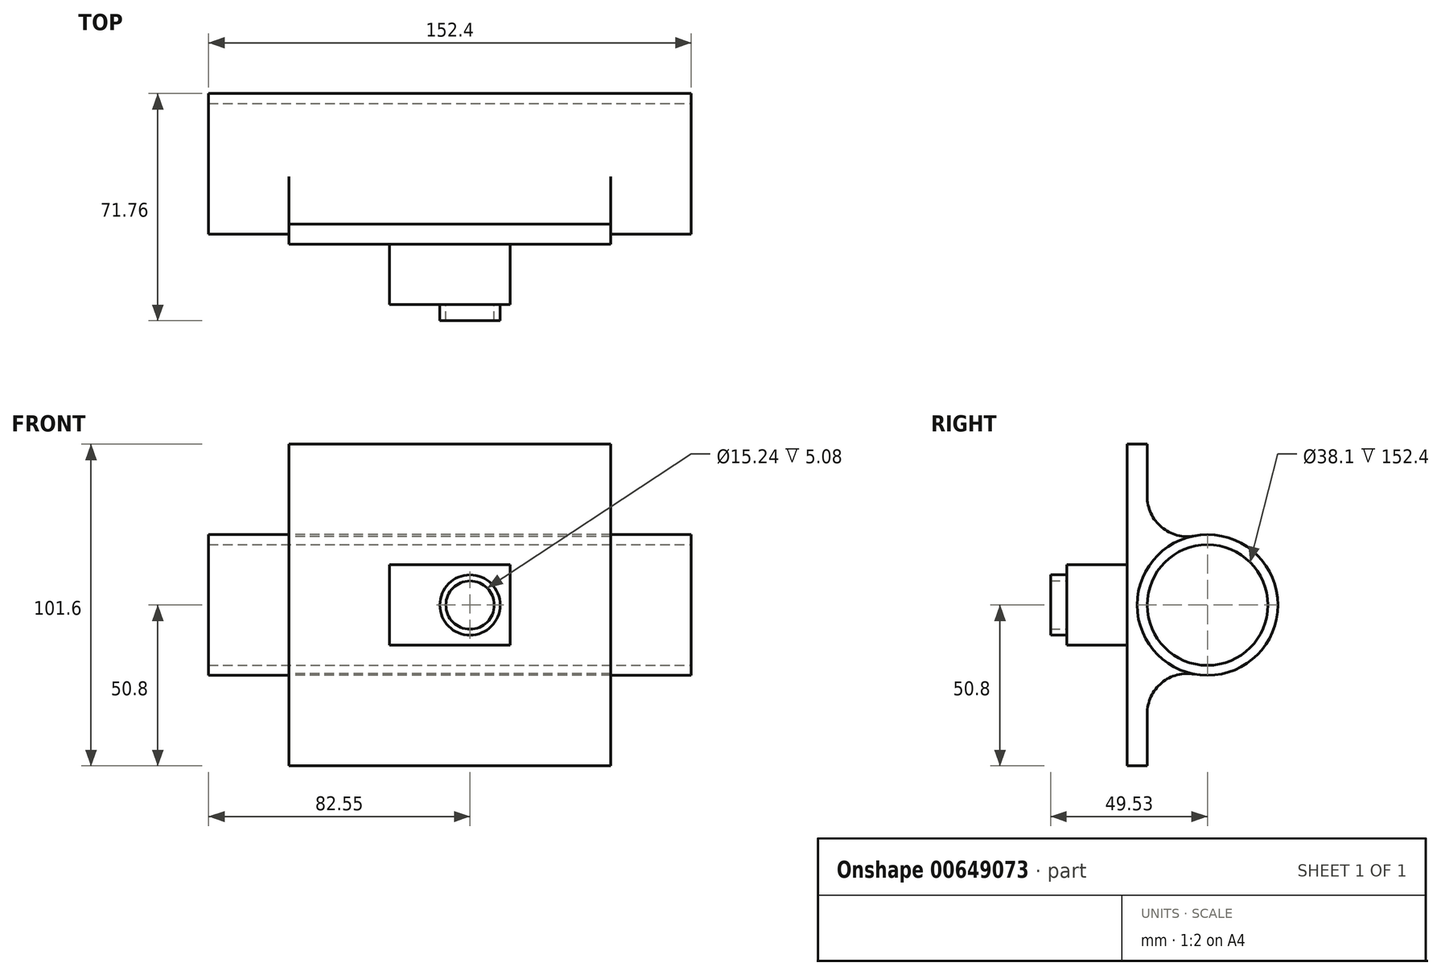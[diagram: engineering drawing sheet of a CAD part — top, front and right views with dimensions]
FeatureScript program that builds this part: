
annotation { "Feature Type Name" : "Feature", "Feature Type Description" : "" }
export const myFeature = defineFeature(function(context is Context, id is Id, definition is map)
    precondition{}
    {
        {
            var Q0;
            Q0=qCreatedBy(makeId("Right.planeOp"),FACE);
            var sketch = newSketch(context, id + "F0", { "sketchPlane" : qUnion([Q0])});
            skCircle(sketch, "E0", {"center": v(0, 0) * mm, "radius": 22.23 * mm});
            skSolve(sketch);
        }
        {
            var Q0;
            Q0 = qSketchRegion(id + "F0", true);
            extrude(context, id + "F1", {"entities" : qUnion([Q0]), "depth" : 76.2 * mm, "offsetDistance" : 25.4 * mm, "hasSecondDirection" : true, "secondDirectionOppositeDirection" : true, "secondDirectionDepth" : 76.2 * mm});
        }
        {
            var Q0;
            Q0=qCreatedBy(makeId("Front.planeOp"),FACE);
            var sketch = newSketch(context, id + "F2", { "sketchPlane" : qUnion([Q0])});
            skLineSegment(sketch, "E1.bottom", {"start": v(-50.8, -50.8) * mm, "end": v(50.8, -50.8) * mm});
            skLineSegment(sketch, "E1.top", {"start": v(-50.8, 50.8) * mm, "end": v(50.8, 50.8) * mm});
            skLineSegment(sketch, "E1.left", {"start": v(-50.8, -50.8) * mm, "end": v(-50.8, 50.8) * mm});
            skLineSegment(sketch, "E1.right", {"start": v(50.8, -50.8) * mm, "end": v(50.8, 50.8) * mm});
            skSolve(sketch);
        }
        {
            var Q0;
            Q0 = qSketchRegion(id + "F2", true);
            extrude(context, id + "F3", {"entities" : qUnion([Q0]), "operationType" : NewBodyOperationType.ADD, "depth" : 25.4 * mm, "offsetDistance" : 25.4 * mm, "hasSecondDirection" : true, "secondDirectionOppositeDirection" : false, "secondDirectionDepth" : 19.05 * mm});
        }
        {
            var Q0;
            Q0=makeQuery(id+"F3.boolean.opBoolean","INTERSECT",EDGE,{"disambiguationData":[OD(1.0)],"derivedFrom":[makeQuery(id+"F1.opExtrude","SWEPT_FACE",FACE,{"disambiguationData":[OSD([sQuery(id+"F0.wireOp",EDGE,"E0")])]}),makeQuery(id+"F3.opExtrude","CAP_FACE",FACE,{"disambiguationData":[OSD([sQuery(id+"F2.wireOp",EDGE,"E1.bottom"),sQuery(id+"F2.wireOp",EDGE,"E1.top"),sQuery(id+"F2.wireOp",EDGE,"E1.left"),sQuery(id+"F2.wireOp",EDGE,"E1.right")])],"isStart":true})]});
            var Q1;
            Q1=makeQuery(id+"F3.boolean.opBoolean","INTERSECT",EDGE,{"disambiguationData":[OD(0.0)],"derivedFrom":[makeQuery(id+"F1.opExtrude","SWEPT_FACE",FACE,{"disambiguationData":[OSD([sQuery(id+"F0.wireOp",EDGE,"E0")])]}),makeQuery(id+"F3.opExtrude","CAP_FACE",FACE,{"disambiguationData":[OSD([sQuery(id+"F2.wireOp",EDGE,"E1.bottom"),sQuery(id+"F2.wireOp",EDGE,"E1.top"),sQuery(id+"F2.wireOp",EDGE,"E1.left"),sQuery(id+"F2.wireOp",EDGE,"E1.right")])],"isStart":true})]});
            fillet(context, id + "F4", {"entities" : qUnion([Q0, Q1]), "radius" : 12.7 * mm, "tangentPropagation" : true, "allowEdgeOverflow" : false});
        }
        {
            var Q0;
            Q0=makeQuery(id+"F3.opExtrude","CAP_FACE",FACE,{"disambiguationData":[OSD([sQuery(id+"F2.wireOp",EDGE,"E1.bottom"),sQuery(id+"F2.wireOp",EDGE,"E1.top"),sQuery(id+"F2.wireOp",EDGE,"E1.left"),sQuery(id+"F2.wireOp",EDGE,"E1.right")])],"isStart":false});
            var sketch = newSketch(context, id + "F5", { "sketchPlane" : qUnion([Q0])});
            skLineSegment(sketch, "E2.bottom", {"start": v(-19.05, -12.7) * mm, "end": v(19.05, -12.7) * mm});
            skLineSegment(sketch, "E2.top", {"start": v(-19.05, 12.7) * mm, "end": v(19.05, 12.7) * mm});
            skLineSegment(sketch, "E2.left", {"start": v(-19.05, -12.7) * mm, "end": v(-19.05, 12.7) * mm});
            skLineSegment(sketch, "E2.right", {"start": v(19.05, -12.7) * mm, "end": v(19.05, 12.7) * mm});
            skSolve(sketch);
        }
        {
            var Q0;
            Q0 = qSketchRegion(id + "F5", true);
            extrude(context, id + "F6", {"entities" : qUnion([Q0]), "operationType" : NewBodyOperationType.ADD, "depth" : 19.05 * mm, "offsetDistance" : 25.4 * mm});
        }
        {
            var Q0;
            Q0=makeQuery(id+"F6.opExtrude","CAP_FACE",FACE,{"disambiguationData":[OSD([sQuery(id+"F5.wireOp",EDGE,"E2.bottom"),sQuery(id+"F5.wireOp",EDGE,"E2.top"),sQuery(id+"F5.wireOp",EDGE,"E2.left"),sQuery(id+"F5.wireOp",EDGE,"E2.right")])],"isStart":false});
            var sketch = newSketch(context, id + "F7", { "sketchPlane" : qUnion([Q0])});
            skCircle(sketch, "E3", {"center": v(6.35, 0) * mm, "radius": 9.53 * mm});
            skCircle(sketch, "E4", {"center": v(6.35, 0) * mm, "radius": 7.62 * mm});
            skSolve(sketch);
        }
        {
            var Q0;
            Q0 = qSketchRegion(id + "F7", true);
            extrude(context, id + "F8", {"entities" : qUnion([Q0]), "operationType" : NewBodyOperationType.ADD, "depth" : 5.08 * mm, "offsetDistance" : 25.4 * mm});
        }
        {
            var Q0;
            Q0=makeQuery(id+"F1.opExtrude","CAP_FACE",FACE,{"disambiguationData":[OSD([sQuery(id+"F0.wireOp",EDGE,"E0")])],"isStart":false});
            var sketch = newSketch(context, id + "F9", { "sketchPlane" : qUnion([Q0])});
            skCircle(sketch, "E5", {"center": v(0, 0) * mm, "radius": 19.05 * mm});
            skSolve(sketch);
        }
        {
            var Q0;
            Q0 = qSketchRegion(id + "F9", true);
            extrude(context, id + "F10", {"entities" : qUnion([Q0]), "operationType" : NewBodyOperationType.REMOVE, "oppositeDirection" : true, "depth" : 152.4 * mm, "offsetDistance" : 25.4 * mm});
        }
    });
